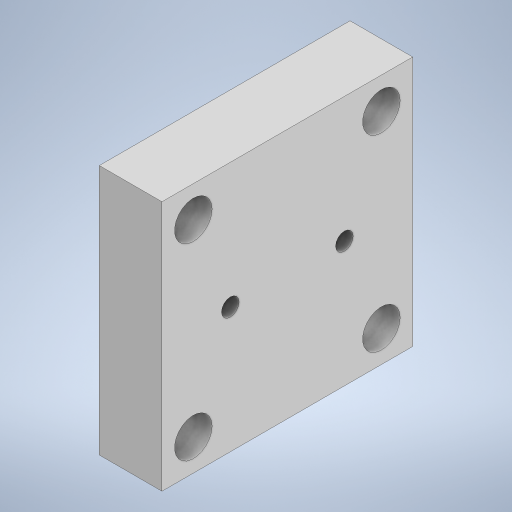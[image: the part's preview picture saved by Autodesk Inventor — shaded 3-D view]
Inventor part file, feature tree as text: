
AUTODESK INVENTOR PART (.ipt)
format: ipt  version: 2023 (Build 270158000, 158)  size: 221,696 bytes
history: native  units: mm
features: extrude x3, sketch x3
ambient origin geometry x8: Origin, YZ Plane, XZ Plane, XY Plane, X Axis, Y Axis, Z Axis, Center Point
bodies: Volumenkörper1 (feature_tree)
feature tree (6):
  extrude  "Extrusion1"  Depth=40.0mm
  extrude  "Extrusion2"  Depth=20.0mm
  extrude  "Extrusion3"  Depth=3.0mm
  sketch  "Skizze1"  dims[d0=40.0mm d1=40.0mm]
  sketch  "Skizze2"  dims[d2=20.0mm d3=20.0mm]
  sketch  "Skizze3"  dims[d4=10.0mm d5=0.0mm d7=6.0mm d8=15.0mm d9=15.0mm d10=3.0mm d11=0.0mm d12=40.0mm d14=360.0deg d16=2.8mm d17=9.1mm d18=3.0mm d19=0.0mm]
